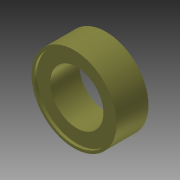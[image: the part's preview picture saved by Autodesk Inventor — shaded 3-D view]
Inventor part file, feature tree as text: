
AUTODESK INVENTOR PART (.ipt)
format: ipt  version: 2012 (Build 160160000, 160)  size: 89,088 bytes
history: native  units: in
note: dims shown in document units (in); Inventor stores cm internally (conversion verified against a paired STEP export)
features: extrude x2, sketch x1
ambient origin geometry x8: Origin, YZ Plane, XZ Plane, XY Plane, X Axis, Y Axis, Z Axis, Center Point
bodies: Solid1 (feature_tree)
feature tree (3):
  sketch  "Sketch1"  dims[d0=1.0in d1=0.9375in d3=0.625in d4=0.375in d5=0.0in d6=0.0325in d7=0.0in]
  extrude  "Extrusion1"  Depth=0.9375in
  extrude  "Extrusion2"  Depth=0.625in
